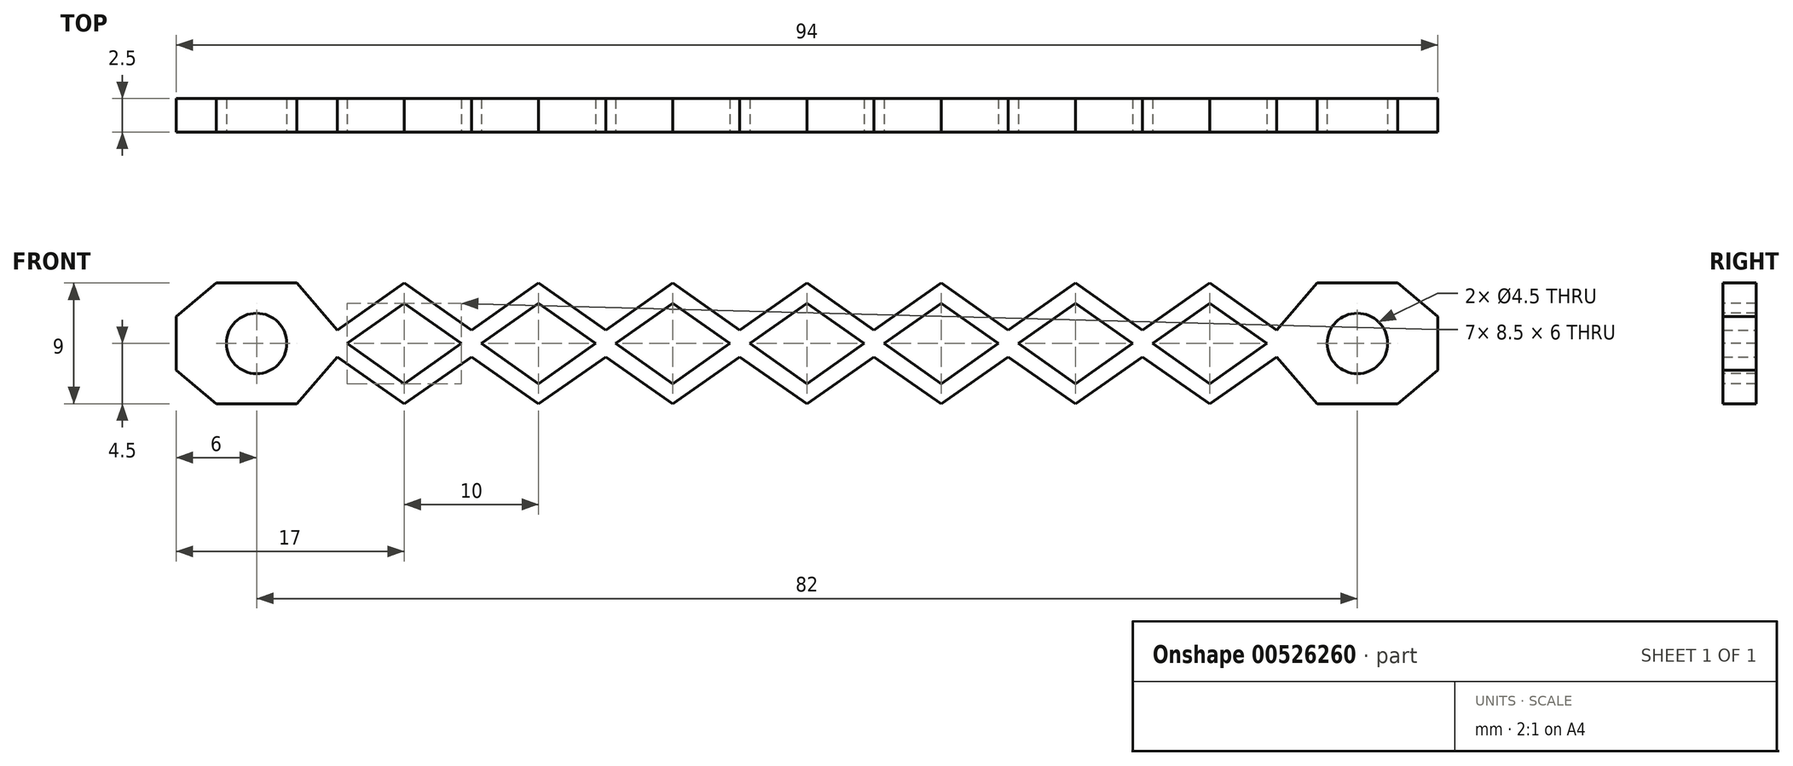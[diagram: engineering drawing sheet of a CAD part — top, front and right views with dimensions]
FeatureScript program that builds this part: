
annotation { "Feature Type Name" : "Feature", "Feature Type Description" : "" }
export const myFeature = defineFeature(function(context is Context, id is Id, definition is map)
    precondition{}
    {
        {
            var Q0;
            Q0=qCreatedBy(makeId("Front.planeOp"),FACE);
            var sketch = newSketch(context, id + "F0", { "sketchPlane" : qUnion([Q0])});
            skLineSegment(sketch, "E0", {"start": v(70, 0) * mm, "end": v(0, 0) * mm});
            skLineSegment(sketch, "E1", {"start": v(5, 4.5) * mm, "end": v(10, 1) * mm});
            skLineSegment(sketch, "E2", {"start": v(10, 1) * mm, "end": v(15, 4.5) * mm});
            skLineSegment(sketch, "E3", {"start": v(15, 4.5) * mm, "end": v(20, 1) * mm});
            skLineSegment(sketch, "E4", {"start": v(20, 1) * mm, "end": v(25, 4.5) * mm});
            skLineSegment(sketch, "E5", {"start": v(25, 4.5) * mm, "end": v(30, 1) * mm});
            skLineSegment(sketch, "E6", {"start": v(30, 1) * mm, "end": v(35, 4.5) * mm});
            skLineSegment(sketch, "E7", {"start": v(35, 4.5) * mm, "end": v(40, 1) * mm});
            skLineSegment(sketch, "E8", {"start": v(40, 1) * mm, "end": v(45, 4.5) * mm});
            skLineSegment(sketch, "E9", {"start": v(45, 4.5) * mm, "end": v(50, 1) * mm});
            skLineSegment(sketch, "E10", {"start": v(50, 1) * mm, "end": v(55, 4.5) * mm});
            skLineSegment(sketch, "E11", {"start": v(55, 4.5) * mm, "end": v(60, 1) * mm});
            skLineSegment(sketch, "E12", {"start": v(60, 1) * mm, "end": v(65, 4.5) * mm});
            skLineSegment(sketch, "E13", {"start": v(5, 4.5) * mm, "end": v(0, 1) * mm});
            skLineSegment(sketch, "E14", {"start": v(65, 4.5) * mm, "end": v(70, 1) * mm});
            skLineSegment(sketch, "E15", {"start": v(0, 1) * mm, "end": v(-3, 4.5) * mm});
            skLineSegment(sketch, "E16", {"start": v(-3, 4.5) * mm, "end": v(-9, 4.5) * mm});
            skLineSegment(sketch, "E17", {"start": v(-12, 2) * mm, "end": v(-12, 0) * mm});
            skLineSegment(sketch, "E18", {"start": v(-12, 0) * mm, "end": v(0, 0) * mm});
            skLineSegment(sketch, "E19", {"start": v(70, 1) * mm, "end": v(73, 4.5) * mm});
            skLineSegment(sketch, "E20", {"start": v(73, 4.5) * mm, "end": v(79, 4.5) * mm});
            skLineSegment(sketch, "E21", {"start": v(82, 2) * mm, "end": v(82, 0) * mm});
            skLineSegment(sketch, "E22", {"start": v(82, 0) * mm, "end": v(70, 0) * mm});
            skLineSegment(sketch, "E23", {"start": v(-12, 2) * mm, "end": v(-9, 4.5) * mm});
            skLineSegment(sketch, "E24", {"start": v(79, 4.5) * mm, "end": v(82, 2) * mm});
            skSolve(sketch);
        }
        {
            var Q0;
            Q0 = qSketchRegion(id + "F0", true);
            extrude(context, id + "F1", {"entities" : qUnion([Q0]), "depth" : 2.5 * mm, "offsetDistance" : 25 * mm});
        }
        {
            var Q0;
            Q0=makeQuery(id+"F1.opExtrude","SWEPT_BODY",BODY,{"disambiguationData":[OSD([sQuery(id+"F0.wireOp",EDGE,"LPwpaLgB-PGL5-g9TU-atmH-A0vsAeZahWsW"),sQuery(id+"F0.wireOp",EDGE,"5aKbtLoZ-XcfF-rQYE-2XJ4-nHQ1WXYjiWf6"),sQuery(id+"F0.wireOp",EDGE,"E0"),sQuery(id+"F0.wireOp",EDGE,"E1"),sQuery(id+"F0.wireOp",EDGE,"E2"),sQuery(id+"F0.wireOp",EDGE,"E3"),sQuery(id+"F0.wireOp",EDGE,"E4"),sQuery(id+"F0.wireOp",EDGE,"E5"),sQuery(id+"F0.wireOp",EDGE,"E6"),sQuery(id+"F0.wireOp",EDGE,"E7"),sQuery(id+"F0.wireOp",EDGE,"E8"),sQuery(id+"F0.wireOp",EDGE,"E9"),sQuery(id+"F0.wireOp",EDGE,"E10"),sQuery(id+"F0.wireOp",EDGE,"E11"),sQuery(id+"F0.wireOp",EDGE,"E12")])]});
            var Q1;
            Q1=qCreatedBy(makeId("Top.planeOp"),FACE);
            mirror(context, id + "F2", {"operationType" : NewBodyOperationType.ADD, "entities" : qUnion([Q0]), "mirrorPlane" : qUnion([Q1])});
        }
        {
            var Q0;
            {var subQ0=makeQuery(id+"F1.opExtrude","CAP_FACE",FACE,{"disambiguationData":[OSD([sQuery(id+"F0.wireOp",EDGE,"E0"),sQuery(id+"F0.wireOp",EDGE,"E1"),sQuery(id+"F0.wireOp",EDGE,"E2"),sQuery(id+"F0.wireOp",EDGE,"E3"),sQuery(id+"F0.wireOp",EDGE,"E4"),sQuery(id+"F0.wireOp",EDGE,"E5"),sQuery(id+"F0.wireOp",EDGE,"E6"),sQuery(id+"F0.wireOp",EDGE,"E7"),sQuery(id+"F0.wireOp",EDGE,"E8"),sQuery(id+"F0.wireOp",EDGE,"E9"),sQuery(id+"F0.wireOp",EDGE,"E10"),sQuery(id+"F0.wireOp",EDGE,"E11"),sQuery(id+"F0.wireOp",EDGE,"E12"),sQuery(id+"F0.wireOp",EDGE,"E13"),sQuery(id+"F0.wireOp",EDGE,"E14"),sQuery(id+"F0.wireOp",EDGE,"E15"),sQuery(id+"F0.wireOp",EDGE,"E16"),sQuery(id+"F0.wireOp",EDGE,"E17"),sQuery(id+"F0.wireOp",EDGE,"E18"),sQuery(id+"F0.wireOp",EDGE,"E19"),sQuery(id+"F0.wireOp",EDGE,"E20"),sQuery(id+"F0.wireOp",EDGE,"E21"),sQuery(id+"F0.wireOp",EDGE,"E22")])],"isStart":false});Q0=makeQuery(id+"F2.boolean.opBoolean","MERGE",FACE,{"derivedFrom":[subQ0,makeQuery(id+"F2.opPattern","COPY",FACE,{"derivedFrom":subQ0,"instanceName":"1"})]});}
            var sketch = newSketch(context, id + "F3", { "sketchPlane" : qUnion([Q0])});
            skLineSegment(sketch, "E25", {"start": v(0.75, 0) * mm, "end": v(5, -3) * mm});
            skLineSegment(sketch, "E26", {"start": v(5, -3) * mm, "end": v(9.25, 0) * mm});
            skLineSegment(sketch, "E27", {"start": v(9.25, 0) * mm, "end": v(5, 3) * mm});
            skLineSegment(sketch, "E28", {"start": v(5, 3) * mm, "end": v(0.75, 0) * mm});
            skLineSegment(sketch, "E29", {"start": v(20.75, 0) * mm, "end": v(25, -3) * mm});
            skLineSegment(sketch, "E30", {"start": v(25, -3) * mm, "end": v(29.25, 0) * mm});
            skLineSegment(sketch, "E31", {"start": v(29.25, 0) * mm, "end": v(25, 3) * mm});
            skLineSegment(sketch, "E32", {"start": v(25, 3) * mm, "end": v(20.75, 0) * mm});
            skLineSegment(sketch, "E33", {"start": v(30.75, 0) * mm, "end": v(35, -3) * mm});
            skLineSegment(sketch, "E34", {"start": v(35, -3) * mm, "end": v(39.25, 0) * mm});
            skLineSegment(sketch, "E35", {"start": v(39.25, 0) * mm, "end": v(35, 3) * mm});
            skLineSegment(sketch, "E36", {"start": v(35, 3) * mm, "end": v(30.75, 0) * mm});
            skLineSegment(sketch, "E37", {"start": v(40.75, 0) * mm, "end": v(45, 3) * mm});
            skLineSegment(sketch, "E38", {"start": v(45, 3) * mm, "end": v(49.25, 0) * mm});
            skLineSegment(sketch, "E39", {"start": v(49.25, 0) * mm, "end": v(45, -3) * mm});
            skLineSegment(sketch, "E40", {"start": v(45, -3) * mm, "end": v(40.75, 0) * mm});
            skLineSegment(sketch, "E41", {"start": v(50.75, 0) * mm, "end": v(55, 3) * mm});
            skLineSegment(sketch, "E42", {"start": v(55, 3) * mm, "end": v(59.25, 0) * mm});
            skLineSegment(sketch, "E43", {"start": v(59.25, 0) * mm, "end": v(55, -3) * mm});
            skLineSegment(sketch, "E44", {"start": v(55, -3) * mm, "end": v(50.75, 0) * mm});
            skLineSegment(sketch, "E45", {"start": v(60.75, 0) * mm, "end": v(65, 3) * mm});
            skLineSegment(sketch, "E46", {"start": v(65, 3) * mm, "end": v(69.25, 0) * mm});
            skLineSegment(sketch, "E47", {"start": v(69.25, 0) * mm, "end": v(65, -3) * mm});
            skLineSegment(sketch, "E48", {"start": v(65, -3) * mm, "end": v(60.75, 0) * mm});
            skLineSegment(sketch, "E49", {"start": v(10.75, 0) * mm, "end": v(15, 3) * mm});
            skLineSegment(sketch, "E50", {"start": v(15, 3) * mm, "end": v(19.25, 0) * mm});
            skLineSegment(sketch, "E51", {"start": v(19.25, 0) * mm, "end": v(15, -3) * mm});
            skLineSegment(sketch, "E52", {"start": v(15, -3) * mm, "end": v(10.75, 0) * mm});
            skSolve(sketch);
        }
        {
            var Q0;
            Q0 = qSketchRegion(id + "F3", true);
            extrude(context, id + "F4", {"entities" : qUnion([Q0]), "operationType" : NewBodyOperationType.REMOVE, "endBound" : BoundingType.UP_TO_NEXT, "oppositeDirection" : true, "depth" : 25 * mm, "offsetDistance" : 25 * mm});
        }
        {
            var Q0;
            {var subQ0=makeQuery(id+"F1.opExtrude","CAP_FACE",FACE,{"disambiguationData":[OSD([sQuery(id+"F0.wireOp",EDGE,"E0"),sQuery(id+"F0.wireOp",EDGE,"E1"),sQuery(id+"F0.wireOp",EDGE,"E2"),sQuery(id+"F0.wireOp",EDGE,"E3"),sQuery(id+"F0.wireOp",EDGE,"E4"),sQuery(id+"F0.wireOp",EDGE,"E5"),sQuery(id+"F0.wireOp",EDGE,"E6"),sQuery(id+"F0.wireOp",EDGE,"E7"),sQuery(id+"F0.wireOp",EDGE,"E8"),sQuery(id+"F0.wireOp",EDGE,"E9"),sQuery(id+"F0.wireOp",EDGE,"E10"),sQuery(id+"F0.wireOp",EDGE,"E11"),sQuery(id+"F0.wireOp",EDGE,"E12"),sQuery(id+"F0.wireOp",EDGE,"E13"),sQuery(id+"F0.wireOp",EDGE,"E14"),sQuery(id+"F0.wireOp",EDGE,"E15"),sQuery(id+"F0.wireOp",EDGE,"E16"),sQuery(id+"F0.wireOp",EDGE,"E17"),sQuery(id+"F0.wireOp",EDGE,"E18"),sQuery(id+"F0.wireOp",EDGE,"E19"),sQuery(id+"F0.wireOp",EDGE,"E20"),sQuery(id+"F0.wireOp",EDGE,"E21"),sQuery(id+"F0.wireOp",EDGE,"E22")])],"isStart":false});Q0=makeQuery(id+"F2.boolean.opBoolean","MERGE",FACE,{"derivedFrom":[subQ0,makeQuery(id+"F2.opPattern","COPY",FACE,{"derivedFrom":subQ0,"instanceName":"1"})]});}
            var sketch = newSketch(context, id + "F5", { "sketchPlane" : qUnion([Q0])});
            skCircle(sketch, "E53", {"center": v(-6, 0) * mm, "radius": 2.25 * mm});
            skPoint(sketch, "E53.centerSnap0", {"position": v(-6, 4.5) * mm});
            skCircle(sketch, "E54", {"center": v(76, 0) * mm, "radius": 2.25 * mm});
            skPoint(sketch, "E54.centerSnap0", {"position": v(76, -4.5) * mm});
            skSolve(sketch);
        }
        {
            var Q0;
            Q0 = qSketchRegion(id + "F5", true);
            extrude(context, id + "F6", {"entities" : qUnion([Q0]), "operationType" : NewBodyOperationType.REMOVE, "endBound" : BoundingType.UP_TO_NEXT, "oppositeDirection" : true, "depth" : 25 * mm, "offsetDistance" : 25 * mm});
        }
    });
